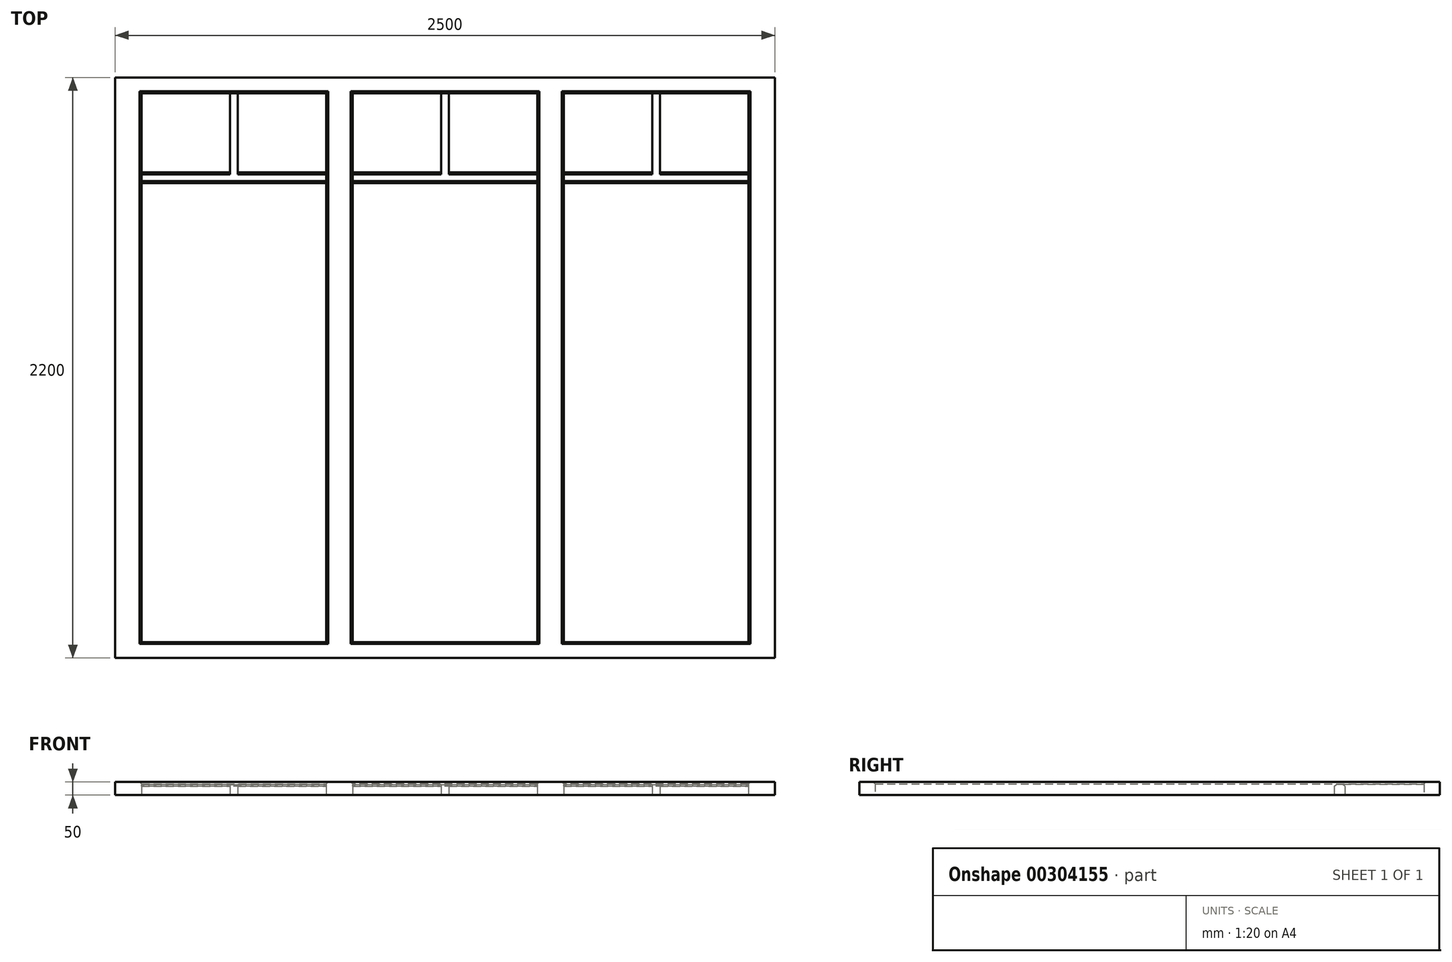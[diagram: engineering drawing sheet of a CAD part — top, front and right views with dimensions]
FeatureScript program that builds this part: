
annotation { "Feature Type Name" : "Feature", "Feature Type Description" : "" }
export const myFeature = defineFeature(function(context is Context, id is Id, definition is map)
    precondition{}
    {
        {
            var Q0;
            Q0=qCreatedBy(makeId("Top.planeOp"),FACE);
            var sketch = newSketch(context, id + "F0", { "sketchPlane" : qUnion([Q0])});
            skLineSegment(sketch, "E0.bottom", {"start": v(-928.9, 755.2) * mm, "end": v(1571.1, 755.2) * mm});
            skLineSegment(sketch, "E0.top", {"start": v(-928.9, -1444.8) * mm, "end": v(1571.1, -1444.8) * mm});
            skLineSegment(sketch, "E0.left", {"start": v(-928.9, 755.2) * mm, "end": v(-928.9, -1444.8) * mm});
            skLineSegment(sketch, "E0.right", {"start": v(1571.1, 755.2) * mm, "end": v(1571.1, -1444.8) * mm});
            skLineSegment(sketch, "E1.bottom", {"start": v(-828.9, 695.2) * mm, "end": v(-128.9, 695.2) * mm});
            skLineSegment(sketch, "E1.top", {"start": v(-828.9, 395.2) * mm, "end": v(-128.9, 395.2) * mm});
            skLineSegment(sketch, "E1.left", {"start": v(-828.9, 695.2) * mm, "end": v(-828.9, 395.2) * mm});
            skLineSegment(sketch, "E1.right", {"start": v(-128.9, 695.2) * mm, "end": v(-128.9, 395.2) * mm});
            skLineSegment(sketch, "E2.bottom", {"start": v(-28.9, 695.2) * mm, "end": v(671.1, 695.2) * mm});
            skLineSegment(sketch, "E2.top", {"start": v(-28.9, 395.2) * mm, "end": v(671.1, 395.2) * mm});
            skLineSegment(sketch, "E2.left", {"start": v(-28.9, 695.2) * mm, "end": v(-28.9, 395.2) * mm});
            skLineSegment(sketch, "E2.right", {"start": v(671.1, 695.2) * mm, "end": v(671.1, 395.2) * mm});
            skLineSegment(sketch, "E3.bottom", {"start": v(-828.9, 355.2) * mm, "end": v(-128.9, 355.2) * mm});
            skLineSegment(sketch, "E3.top", {"start": v(-828.9, -1384.8) * mm, "end": v(-128.9, -1384.8) * mm});
            skLineSegment(sketch, "E3.left", {"start": v(-828.9, 355.2) * mm, "end": v(-828.9, -1384.8) * mm});
            skLineSegment(sketch, "E3.right", {"start": v(-128.9, 355.2) * mm, "end": v(-128.9, -1384.8) * mm});
            skLineSegment(sketch, "E4.bottom", {"start": v(-28.9, 355.2) * mm, "end": v(671.1, 355.2) * mm});
            skLineSegment(sketch, "E4.top", {"start": v(-28.9, -1384.8) * mm, "end": v(671.1, -1384.8) * mm});
            skLineSegment(sketch, "E4.left", {"start": v(-28.9, 355.2) * mm, "end": v(-28.9, -1384.8) * mm});
            skLineSegment(sketch, "E4.right", {"start": v(671.1, 355.2) * mm, "end": v(671.1, -1384.8) * mm});
            skLineSegment(sketch, "E5.bottom", {"start": v(771.1, 355.2) * mm, "end": v(1471.1, 355.2) * mm});
            skLineSegment(sketch, "E5.top", {"start": v(771.1, -1384.8) * mm, "end": v(1471.1, -1384.8) * mm});
            skLineSegment(sketch, "E5.left", {"start": v(771.1, 355.2) * mm, "end": v(771.1, -1384.8) * mm});
            skLineSegment(sketch, "E5.right", {"start": v(1471.1, 355.2) * mm, "end": v(1471.1, -1384.8) * mm});
            skLineSegment(sketch, "E6.bottom", {"start": v(771.1, 695.2) * mm, "end": v(1471.1, 695.2) * mm});
            skLineSegment(sketch, "E6.top", {"start": v(771.1, 395.2) * mm, "end": v(1471.1, 395.2) * mm});
            skLineSegment(sketch, "E6.left", {"start": v(771.1, 695.2) * mm, "end": v(771.1, 395.2) * mm});
            skLineSegment(sketch, "E6.right", {"start": v(1471.1, 695.2) * mm, "end": v(1471.1, 395.2) * mm});
            skLineSegment(sketch, "E7", {"start": v(-828.9, 395.2) * mm, "end": v(-828.9, 355.2) * mm});
            skLineSegment(sketch, "E8", {"start": v(-128.9, -1384.8) * mm, "end": v(-28.9, -1384.8) * mm});
            skLineSegment(sketch, "E9", {"start": v(671.1, -1384.8) * mm, "end": v(771.1, -1384.8) * mm});
            skLineSegment(sketch, "E10", {"start": v(1471.1, 355.2) * mm, "end": v(1471.1, 395.2) * mm});
            skLineSegment(sketch, "E11", {"start": v(771.1, 695.2) * mm, "end": v(671.1, 695.2) * mm});
            skLineSegment(sketch, "E12", {"start": v(-28.9, 695.2) * mm, "end": v(-128.9, 695.2) * mm});
            skLineSegment(sketch, "E13", {"start": v(-128.9, 395.2) * mm, "end": v(-128.9, 355.2) * mm});
            skLineSegment(sketch, "E14", {"start": v(-28.9, 395.2) * mm, "end": v(-28.9, 355.2) * mm});
            skLineSegment(sketch, "E15", {"start": v(671.1, 395.2) * mm, "end": v(671.1, 355.2) * mm});
            skLineSegment(sketch, "E16", {"start": v(771.1, 395.2) * mm, "end": v(771.1, 355.2) * mm});
            skLineSegment(sketch, "E17", {"start": v(-493.9, 395.2) * mm, "end": v(-493.9, 695.2) * mm});
            skLineSegment(sketch, "E18", {"start": v(-463.9, 695.2) * mm, "end": v(-463.9, 395.2) * mm});
            skLineSegment(sketch, "E19", {"start": v(306.1, 695.2) * mm, "end": v(306.1, 395.2) * mm});
            skLineSegment(sketch, "E20", {"start": v(336.1, 695.2) * mm, "end": v(336.1, 395.2) * mm});
            skLineSegment(sketch, "E21", {"start": v(1106.1, 695.2) * mm, "end": v(1106.1, 395.2) * mm});
            skLineSegment(sketch, "E22", {"start": v(1136.1, 695.2) * mm, "end": v(1136.1, 395.2) * mm});
            skSolve(sketch);
        }
        {
            var Q0;
            Q0=makeQuery(id+"F0.imprint","IMPRINT",FACE,{"disambiguationData":[TD([[makeQuery(id+"F0.imprint","IMPRINT",EDGE,{"derivedFrom":sQuery(id+"F0.wireOp",EDGE,"E0.bottom")}),-1.0]])]});
            var Q1;
            Q1=makeQuery(id+"F0.imprint","IMPRINT",FACE,{"disambiguationData":[TD([[makeQuery(id+"F0.imprint","IMPRINT",EDGE,{"derivedFrom":sQuery(id+"F0.wireOp",EDGE,"E1.right")}),1.0]])]});
            var Q2;
            Q2=makeQuery(id+"F0.imprint","IMPRINT",FACE,{"disambiguationData":[TD([[makeQuery(id+"F0.imprint","IMPRINT",EDGE,{"derivedFrom":sQuery(id+"F0.wireOp",EDGE,"E2.right")}),1.0]])]});
            extrude(context, id + "F1", {"entities" : qUnion([Q0, Q1, Q2]), "depth" : 50 * mm, "offsetDistance" : 25 * mm});
        }
        {
            var Q0;
            Q0=makeQuery(id+"F0.imprint","IMPRINT",FACE,{"disambiguationData":[TD([[makeQuery(id+"F0.imprint","IMPRINT",EDGE,{"derivedFrom":sQuery(id+"F0.wireOp",EDGE,"E1.top")}),-1.0]])]});
            var Q1;
            Q1=makeQuery(id+"F0.imprint","IMPRINT",FACE,{"disambiguationData":[TD([[makeQuery(id+"F0.imprint","IMPRINT",EDGE,{"derivedFrom":sQuery(id+"F0.wireOp",EDGE,"E4.bottom")}),1.0]])]});
            var Q2;
            Q2=makeQuery(id+"F0.imprint","IMPRINT",FACE,{"disambiguationData":[TD([[makeQuery(id+"F0.imprint","IMPRINT",EDGE,{"derivedFrom":sQuery(id+"F0.wireOp",EDGE,"E5.bottom")}),1.0]])]});
            var Q3;
            {var subQ0=sQuery(id+"F0.wireOp",EDGE,"E21");Q3=makeQuery(id+"F0.imprint","IMPRINT",FACE,{"disambiguationData":[TD([[makeQuery(id+"F0.imprint","IMPRINT",EDGE,{"derivedFrom":subQ0}),1.0]])]});}
            var Q4;
            {var subQ0=sQuery(id+"F0.wireOp",EDGE,"E19");Q4=makeQuery(id+"F0.imprint","IMPRINT",FACE,{"disambiguationData":[TD([[makeQuery(id+"F0.imprint","IMPRINT",EDGE,{"derivedFrom":subQ0}),1.0]])]});}
            var Q5;
            {var subQ0=sQuery(id+"F0.wireOp",EDGE,"E17");Q5=makeQuery(id+"F0.imprint","IMPRINT",FACE,{"disambiguationData":[TD([[makeQuery(id+"F0.imprint","IMPRINT",EDGE,{"derivedFrom":subQ0}),-1.0]])]});}
            extrude(context, id + "F2", {"entities" : qUnion([Q0, Q1, Q2, Q3, Q4, Q5]), "depth" : 40 * mm, "offsetDistance" : 25 * mm});
        }
        {
            var Q0;
            Q0=makeQuery(id+"F1.opExtrude","CAP_EDGE",EDGE,{"disambiguationData":[OSD([sQuery(id+"F0.wireOp",EDGE,"ytPpMPqZ-kEHr-QmaY-d1DR-AzYH62YFSOlj.left")])],"isStart":false});
            var Q1;
            Q1=makeQuery(id+"F1.opExtrude","CAP_EDGE",EDGE,{"disambiguationData":[OSD([sQuery(id+"F0.wireOp",EDGE,"ytPpMPqZ-kEHr-QmaY-d1DR-AzYH62YFSOlj.bottom")])],"isStart":false});
            var Q2;
            Q2=makeQuery(id+"F1.opExtrude","CAP_EDGE",EDGE,{"disambiguationData":[OSD([sQuery(id+"F0.wireOp",EDGE,"ytPpMPqZ-kEHr-QmaY-d1DR-AzYH62YFSOlj.right")])],"isStart":false});
            var Q3;
            Q3=makeQuery(id+"F1.opExtrude","CAP_EDGE",EDGE,{"disambiguationData":[OSD([sQuery(id+"F0.wireOp",EDGE,"ytPpMPqZ-kEHr-QmaY-d1DR-AzYH62YFSOlj.top")])],"isStart":false});
            var Q4;
            Q4=makeQuery(id+"F1.opExtrude","CAP_EDGE",EDGE,{"disambiguationData":[OSD([sQuery(id+"F0.wireOp",EDGE,"r7QiBjje-UKbf-qYST-CBBd-TYCSkPhiPhca.top")])],"isStart":false});
            var Q5;
            Q5=makeQuery(id+"F1.opExtrude","CAP_EDGE",EDGE,{"disambiguationData":[OSD([sQuery(id+"F0.wireOp",EDGE,"r7QiBjje-UKbf-qYST-CBBd-TYCSkPhiPhca.bottom")])],"isStart":false});
            var Q6;
            Q6=makeQuery(id+"F1.opExtrude","CAP_EDGE",EDGE,{"disambiguationData":[OSD([sQuery(id+"F0.wireOp",EDGE,"r7QiBjje-UKbf-qYST-CBBd-TYCSkPhiPhca.left")])],"isStart":false});
            var Q7;
            Q7=makeQuery(id+"F1.opExtrude","CAP_EDGE",EDGE,{"disambiguationData":[OSD([sQuery(id+"F0.wireOp",EDGE,"r7QiBjje-UKbf-qYST-CBBd-TYCSkPhiPhca.right")])],"isStart":false});
            var Q8;
            Q8=makeQuery(id+"F1.opExtrude","CAP_EDGE",EDGE,{"disambiguationData":[OSD([sQuery(id+"F0.wireOp",EDGE,"HfWFaPNu-mQyP-ler6-jSu7-HC3u6uNNGoQA.left")])],"isStart":false});
            var Q9;
            Q9=makeQuery(id+"F1.opExtrude","CAP_EDGE",EDGE,{"disambiguationData":[OSD([sQuery(id+"F0.wireOp",EDGE,"HfWFaPNu-mQyP-ler6-jSu7-HC3u6uNNGoQA.bottom")])],"isStart":false});
            var Q10;
            Q10=makeQuery(id+"F1.opExtrude","CAP_EDGE",EDGE,{"disambiguationData":[OSD([sQuery(id+"F0.wireOp",EDGE,"HfWFaPNu-mQyP-ler6-jSu7-HC3u6uNNGoQA.right")])],"isStart":false});
            var Q11;
            Q11=makeQuery(id+"F1.opExtrude","CAP_EDGE",EDGE,{"disambiguationData":[OSD([sQuery(id+"F0.wireOp",EDGE,"HfWFaPNu-mQyP-ler6-jSu7-HC3u6uNNGoQA.top")])],"isStart":false});
            var Q12;
            Q12=makeQuery(id+"F1.opExtrude","CAP_EDGE",EDGE,{"disambiguationData":[OSD([sQuery(id+"F0.wireOp",EDGE,"5wbdZzbv-KT36-aS9W-tHdP-7188U3jB6Ytn.bottom")])],"isStart":false});
            var Q13;
            Q13=makeQuery(id+"F1.opExtrude","CAP_EDGE",EDGE,{"disambiguationData":[OSD([sQuery(id+"F0.wireOp",EDGE,"5wbdZzbv-KT36-aS9W-tHdP-7188U3jB6Ytn.left")])],"isStart":false});
            var Q14;
            Q14=makeQuery(id+"F1.opExtrude","CAP_EDGE",EDGE,{"disambiguationData":[OSD([sQuery(id+"F0.wireOp",EDGE,"5wbdZzbv-KT36-aS9W-tHdP-7188U3jB6Ytn.top")])],"isStart":false});
            var Q15;
            Q15=makeQuery(id+"F1.opExtrude","CAP_EDGE",EDGE,{"disambiguationData":[OSD([sQuery(id+"F0.wireOp",EDGE,"5wbdZzbv-KT36-aS9W-tHdP-7188U3jB6Ytn.right")])],"isStart":false});
            var Q16;
            Q16=makeQuery(id+"F1.opExtrude","CAP_EDGE",EDGE,{"disambiguationData":[OSD([sQuery(id+"F0.wireOp",EDGE,"DTlHMEbU-aPmp-yZgJ-OWsR-Co97d6l2honQ.bottom")])],"isStart":false});
            var Q17;
            Q17=makeQuery(id+"F1.opExtrude","CAP_EDGE",EDGE,{"disambiguationData":[OSD([sQuery(id+"F0.wireOp",EDGE,"DTlHMEbU-aPmp-yZgJ-OWsR-Co97d6l2honQ.right")])],"isStart":false});
            var Q18;
            Q18=makeQuery(id+"F1.opExtrude","CAP_EDGE",EDGE,{"disambiguationData":[OSD([sQuery(id+"F0.wireOp",EDGE,"DTlHMEbU-aPmp-yZgJ-OWsR-Co97d6l2honQ.top")])],"isStart":false});
            var Q19;
            Q19=makeQuery(id+"F1.opExtrude","CAP_EDGE",EDGE,{"disambiguationData":[OSD([sQuery(id+"F0.wireOp",EDGE,"DTlHMEbU-aPmp-yZgJ-OWsR-Co97d6l2honQ.left")])],"isStart":false});
            var Q20;
            Q20=makeQuery(id+"F1.opExtrude","CAP_EDGE",EDGE,{"disambiguationData":[OSD([sQuery(id+"F0.wireOp",EDGE,"KnIwFXTZ-7AYv-IQ4P-MqQU-q16PSDZZjzCm.right")])],"isStart":false});
            var Q21;
            Q21=makeQuery(id+"F1.opExtrude","CAP_EDGE",EDGE,{"disambiguationData":[OSD([sQuery(id+"F0.wireOp",EDGE,"KnIwFXTZ-7AYv-IQ4P-MqQU-q16PSDZZjzCm.bottom")])],"isStart":false});
            var Q22;
            Q22=makeQuery(id+"F1.opExtrude","CAP_EDGE",EDGE,{"disambiguationData":[OSD([sQuery(id+"F0.wireOp",EDGE,"KnIwFXTZ-7AYv-IQ4P-MqQU-q16PSDZZjzCm.left")])],"isStart":false});
            var Q23;
            Q23=makeQuery(id+"F1.opExtrude","CAP_EDGE",EDGE,{"disambiguationData":[OSD([sQuery(id+"F0.wireOp",EDGE,"KnIwFXTZ-7AYv-IQ4P-MqQU-q16PSDZZjzCm.top")])],"isStart":false});
            var Q24;
            Q24=makeQuery(id+"F1.opExtrude","CAP_EDGE",EDGE,{"disambiguationData":[OSD([sQuery(id+"F0.wireOp",EDGE,"E1.left")])],"isStart":false});
            var Q25;
            Q25=makeQuery(id+"F1.opExtrude","CAP_EDGE",EDGE,{"disambiguationData":[OSD([sQuery(id+"F0.wireOp",EDGE,"E1.bottom")])],"isStart":false});
            var Q26;
            Q26=makeQuery(id+"F1.opExtrude","CAP_EDGE",EDGE,{"disambiguationData":[OSD([sQuery(id+"F0.wireOp",EDGE,"E1.right")])],"isStart":false});
            var Q27;
            Q27=makeQuery(id+"F1.opExtrude","CAP_EDGE",EDGE,{"disambiguationData":[OSD([sQuery(id+"F0.wireOp",EDGE,"2C36mqMa-A4eQ-qRDU-Ah7K-ji7NIf0B9ti7.left")])],"isStart":false});
            var Q28;
            Q28=makeQuery(id+"F1.opExtrude","CAP_EDGE",EDGE,{"disambiguationData":[OSD([sQuery(id+"F0.wireOp",EDGE,"2C36mqMa-A4eQ-qRDU-Ah7K-ji7NIf0B9ti7.bottom")])],"isStart":false});
            var Q29;
            Q29=makeQuery(id+"F1.opExtrude","CAP_EDGE",EDGE,{"disambiguationData":[OSD([sQuery(id+"F0.wireOp",EDGE,"2C36mqMa-A4eQ-qRDU-Ah7K-ji7NIf0B9ti7.right")])],"isStart":false});
            var Q30;
            Q30=makeQuery(id+"F1.opExtrude","CAP_EDGE",EDGE,{"disambiguationData":[OSD([sQuery(id+"F0.wireOp",EDGE,"E2.left")])],"isStart":false});
            var Q31;
            Q31=makeQuery(id+"F1.opExtrude","CAP_EDGE",EDGE,{"disambiguationData":[OSD([sQuery(id+"F0.wireOp",EDGE,"E2.bottom")])],"isStart":false});
            var Q32;
            Q32=makeQuery(id+"F1.opExtrude","CAP_EDGE",EDGE,{"disambiguationData":[OSD([sQuery(id+"F0.wireOp",EDGE,"E5.left")])],"isStart":false});
            var Q33;
            Q33=makeQuery(id+"F1.opExtrude","CAP_EDGE",EDGE,{"disambiguationData":[OSD([sQuery(id+"F0.wireOp",EDGE,"E5.bottom")])],"isStart":false});
            var Q34;
            Q34=makeQuery(id+"F1.opExtrude","CAP_EDGE",EDGE,{"disambiguationData":[OSD([sQuery(id+"F0.wireOp",EDGE,"E4.bottom")])],"isStart":false});
            var Q35;
            Q35=makeQuery(id+"F1.opExtrude","CAP_EDGE",EDGE,{"disambiguationData":[OSD([sQuery(id+"F0.wireOp",EDGE,"E4.left")])],"isStart":false});
            var Q36;
            Q36=makeQuery(id+"F1.opExtrude","CAP_EDGE",EDGE,{"disambiguationData":[OSD([sQuery(id+"F0.wireOp",EDGE,"E3.right")])],"isStart":false});
            var Q37;
            Q37=makeQuery(id+"F1.opExtrude","CAP_EDGE",EDGE,{"disambiguationData":[OSD([sQuery(id+"F0.wireOp",EDGE,"E3.bottom")])],"isStart":false});
            var Q38;
            Q38=makeQuery(id+"F1.opExtrude","CAP_EDGE",EDGE,{"disambiguationData":[OSD([sQuery(id+"F0.wireOp",EDGE,"E3.left")])],"isStart":false});
            var Q39;
            Q39=makeQuery(id+"F1.opExtrude","CAP_EDGE",EDGE,{"disambiguationData":[OSD([sQuery(id+"F0.wireOp",EDGE,"E2.right")])],"isStart":false});
            var Q40;
            Q40=makeQuery(id+"F1.opExtrude","CAP_EDGE",EDGE,{"disambiguationData":[OSD([sQuery(id+"F0.wireOp",EDGE,"E5.right")])],"isStart":false});
            var Q41;
            Q41=makeQuery(id+"F1.opExtrude","CAP_EDGE",EDGE,{"disambiguationData":[OSD([sQuery(id+"F0.wireOp",EDGE,"E2.top")])],"isStart":false});
            var Q42;
            Q42=makeQuery(id+"F1.opExtrude","CAP_EDGE",EDGE,{"disambiguationData":[OSD([sQuery(id+"F0.wireOp",EDGE,"2C36mqMa-A4eQ-qRDU-Ah7K-ji7NIf0B9ti7.top")])],"isStart":false});
            var Q43;
            Q43=makeQuery(id+"F1.opExtrude","CAP_EDGE",EDGE,{"disambiguationData":[OSD([sQuery(id+"F0.wireOp",EDGE,"E1.top")])],"isStart":false});
            var Q44;
            Q44=makeQuery(id+"F1.opExtrude","CAP_EDGE",EDGE,{"disambiguationData":[OSD([sQuery(id+"F0.wireOp",EDGE,"E4.top")])],"isStart":false});
            var Q45;
            Q45=makeQuery(id+"F1.opExtrude","CAP_EDGE",EDGE,{"disambiguationData":[OSD([sQuery(id+"F0.wireOp",EDGE,"E5.top")])],"isStart":false});
            var Q46;
            Q46=makeQuery(id+"F1.opExtrude","CAP_EDGE",EDGE,{"disambiguationData":[OSD([sQuery(id+"F0.wireOp",EDGE,"E3.top")])],"isStart":false});
            var Q47;
            Q47=makeQuery(id+"F1.opExtrude","CAP_EDGE",EDGE,{"disambiguationData":[OSD([sQuery(id+"F0.wireOp",EDGE,"E6.left")])],"isStart":false});
            var Q48;
            Q48=makeQuery(id+"F1.opExtrude","CAP_EDGE",EDGE,{"disambiguationData":[OSD([sQuery(id+"F0.wireOp",EDGE,"E6.bottom")])],"isStart":false});
            var Q49;
            Q49=makeQuery(id+"F1.opExtrude","CAP_EDGE",EDGE,{"disambiguationData":[OSD([sQuery(id+"F0.wireOp",EDGE,"E6.right")])],"isStart":false});
            var Q50;
            Q50=makeQuery(id+"F1.opExtrude","CAP_EDGE",EDGE,{"disambiguationData":[OSD([sQuery(id+"F0.wireOp",EDGE,"E6.top")])],"isStart":false});
            var Q51;
            Q51=makeQuery(id+"F2.opExtrude","CAP_EDGE",EDGE,{"disambiguationData":[OSD([sQuery(id+"F0.wireOp",EDGE,"E3.bottom")])],"isStart":false});
            var Q52;
            Q52=makeQuery(id+"F2.opExtrude","CAP_EDGE",EDGE,{"disambiguationData":[OSD([sQuery(id+"F0.wireOp",EDGE,"E4.bottom")])],"isStart":false});
            var Q53;
            Q53=makeQuery(id+"F2.opExtrude","CAP_EDGE",EDGE,{"disambiguationData":[OSD([sQuery(id+"F0.wireOp",EDGE,"E4.left")])],"isStart":false});
            var Q54;
            Q54=makeQuery(id+"F2.opExtrude","CAP_EDGE",EDGE,{"disambiguationData":[OSD([sQuery(id+"F0.wireOp",EDGE,"E5.left")])],"isStart":false});
            var Q55;
            Q55=makeQuery(id+"F2.opExtrude","CAP_EDGE",EDGE,{"disambiguationData":[OSD([sQuery(id+"F0.wireOp",EDGE,"E6.left")])],"isStart":false});
            var Q56;
            Q56=makeQuery(id+"F2.opExtrude","CAP_EDGE",EDGE,{"disambiguationData":[OSD([sQuery(id+"F0.wireOp",EDGE,"E2.left")])],"isStart":false});
            var Q57;
            Q57=makeQuery(id+"F2.opExtrude","CAP_EDGE",EDGE,{"disambiguationData":[OSD([sQuery(id+"F0.wireOp",EDGE,"E3.right")])],"isStart":false});
            var Q58;
            Q58=makeQuery(id+"F2.opExtrude","CAP_EDGE",EDGE,{"disambiguationData":[OSD([sQuery(id+"F0.wireOp",EDGE,"E1.right")])],"isStart":false});
            var Q59;
            Q59=makeQuery(id+"F2.opExtrude","CAP_EDGE",EDGE,{"disambiguationData":[OSD([sQuery(id+"F0.wireOp",EDGE,"E1.top")])],"isStart":false});
            var Q60;
            Q60=makeQuery(id+"F2.opExtrude","CAP_EDGE",EDGE,{"disambiguationData":[OSD([sQuery(id+"F0.wireOp",EDGE,"E2.top")])],"isStart":false});
            var Q61;
            Q61=makeQuery(id+"F2.opExtrude","CAP_EDGE",EDGE,{"disambiguationData":[OSD([sQuery(id+"F0.wireOp",EDGE,"E6.top")])],"isStart":false});
            var Q62;
            Q62=makeQuery(id+"F2.opExtrude","CAP_EDGE",EDGE,{"disambiguationData":[OSD([sQuery(id+"F0.wireOp",EDGE,"E5.bottom")])],"isStart":false});
            var Q63;
            Q63=makeQuery(id+"F2.opExtrude","CAP_EDGE",EDGE,{"disambiguationData":[OSD([sQuery(id+"F0.wireOp",EDGE,"E4.right")])],"isStart":false});
            var Q64;
            Q64=makeQuery(id+"F2.opExtrude","CAP_EDGE",EDGE,{"disambiguationData":[OSD([sQuery(id+"F0.wireOp",EDGE,"E2.right")])],"isStart":false});
            chamfer(context, id + "F3", {"entities" : qUnion([Q0, Q1, Q2, Q3, Q4, Q5, Q6, Q7, Q8, Q9, Q10, Q11, Q12, Q13, Q14, Q15, Q16, Q17, Q18, Q19, Q20, Q21, Q22, Q23, Q24, Q25, Q26, Q27, Q28, Q29, Q30, Q31, Q32, Q33, Q34, Q35, Q36, Q37, Q38, Q39, Q40, Q41, Q42, Q43, Q44, Q45, Q46, Q47, Q48, Q49, Q50, Q51, Q52, Q53, Q54, Q55, Q56, Q57, Q58, Q59, Q60, Q61, Q62, Q63, Q64]), "width" : 7 * mm, "tangentPropagation" : true});
        }
    });
